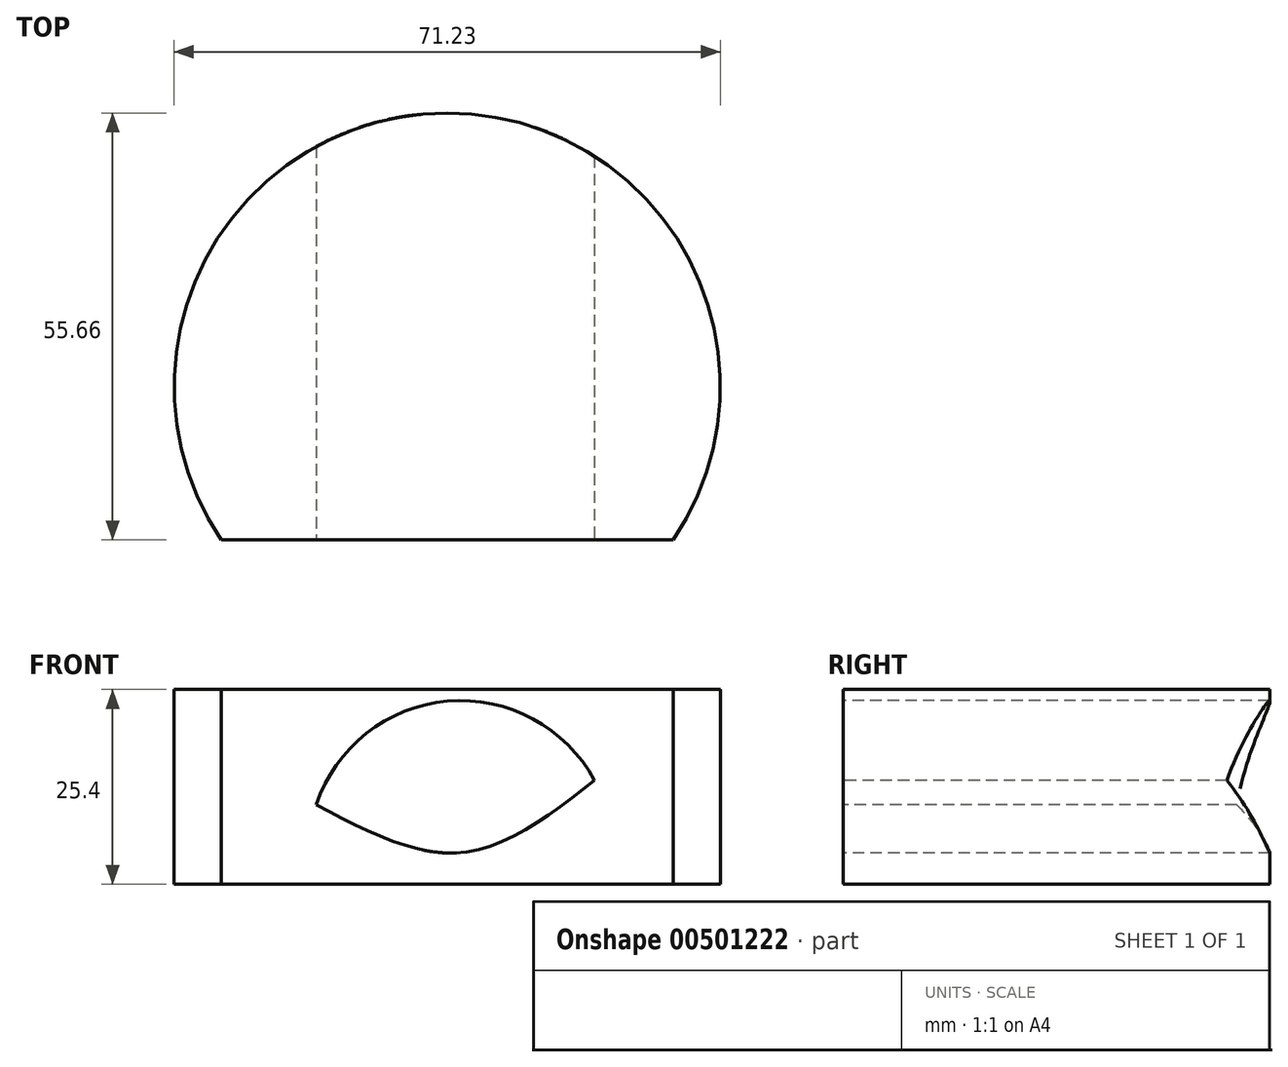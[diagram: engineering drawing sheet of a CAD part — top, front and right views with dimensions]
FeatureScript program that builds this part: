
annotation { "Feature Type Name" : "Feature", "Feature Type Description" : "" }
export const myFeature = defineFeature(function(context is Context, id is Id, definition is map)
    precondition{}
    {
        {
            var Q0;
            Q0=qCreatedBy(makeId("Top.planeOp"),FACE);
            var sketch = newSketch(context, id + "F0", { "sketchPlane" : qUnion([Q0])});
            skArc(sketch, "E0", {"start": v(58.87, 0) * mm, "mid": v(29.44, 55.66) * mm, "end": v(0, 0) * mm});
            skLineSegment(sketch, "E1", {"start": v(0, 0) * mm, "end": v(58.87, 0) * mm});
            skSolve(sketch);
        }
        {
            var Q0;
            Q0 = qSketchRegion(id + "F0", true);
            extrude(context, id + "F1", {"entities" : qUnion([Q0]), "depth" : 25.4 * mm});
        }
        {
            var Q0;
            Q0=makeQuery(id+"F1.opExtrude","SWEPT_FACE",FACE,{"disambiguationData":[OSD([sQuery(id+"F0.wireOp",EDGE,"E1")])]});
            var sketch = newSketch(context, id + "F2", { "sketchPlane" : qUnion([Q0])});
            skArc(sketch, "E2", {"start": v(48.64, 13.53) * mm, "mid": v(29.47, 23.88) * mm, "end": v(12.38, 10.36) * mm});
            skFitSpline(sketch, "E3", {"points": [v(12.38, 10.36) * mm, v(31.19, 4.14) * mm, v(48.64, 13.53) * mm], "startDerivative": vector(38.3, -20.26) * mm, "endDerivative": vector(34.22, 26.59) * mm});
            skSolve(sketch);
        }
        {
            var Q0;
            Q0 = qSketchRegion(id + "F2", true);
            extrude(context, id + "F3", {"entities" : qUnion([Q0]), "operationType" : NewBodyOperationType.REMOVE, "oppositeDirection" : true, "depth" : 59.18 * mm});
        }
    });
